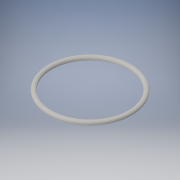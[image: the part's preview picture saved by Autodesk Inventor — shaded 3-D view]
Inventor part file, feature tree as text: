
AUTODESK INVENTOR PART (.ipt)
format: ipt  version: 2016 (Build 200138000, 138)  size: 116,736 bytes
history: native  units: in
note: dims shown in document units (in); Inventor stores cm internally (conversion verified against a paired STEP export)
features: revolve x1, sketch x1
ambient origin geometry x8: Origin, YZ Plane, XZ Plane, XY Plane, X Axis, Y Axis, Z Axis, Center Point
bodies: Solid1 (feature_tree)
feature tree (2):
  revolve  "Revolution1"  [1 undecoded]
  sketch  "Sketch1"  dims[d0=2.42in d1=1.21in d2=0.13in d3=90.0deg]
note: 1 required parameter value undecoded (feature->parameter linkage not recoverable at this tier; creation-order binding heuristic only, values carry confidence <= 0.55)
